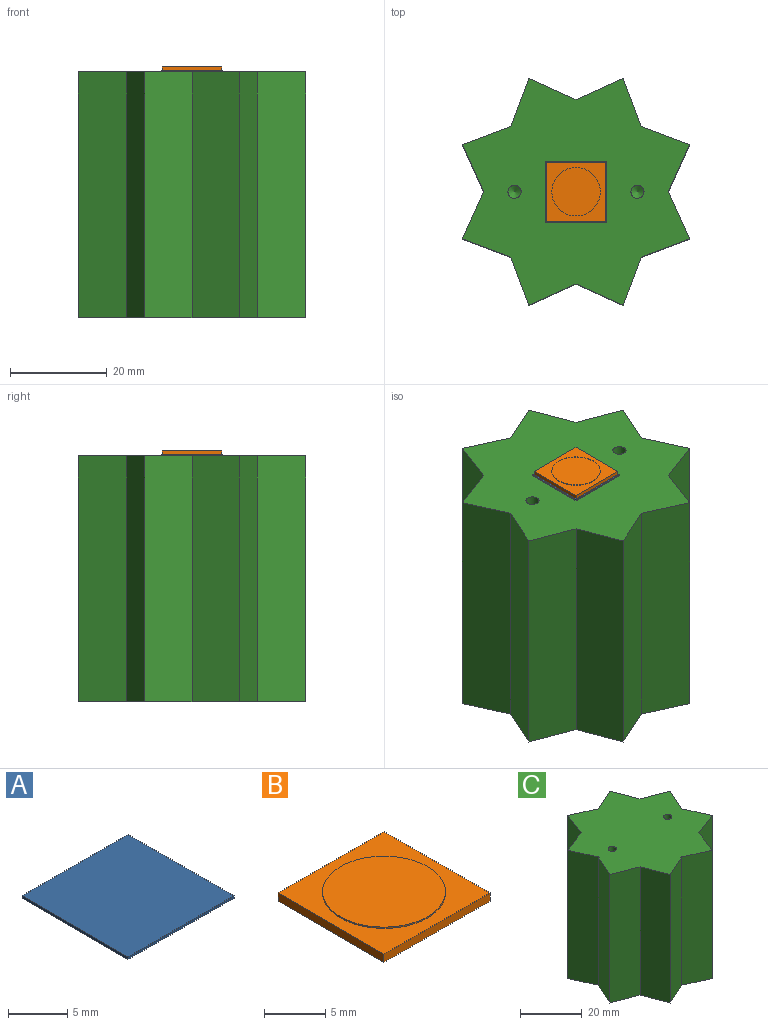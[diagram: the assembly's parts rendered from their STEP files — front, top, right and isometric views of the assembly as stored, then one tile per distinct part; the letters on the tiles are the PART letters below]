
ASSEMBLY  parts=3 mates=2
PART A: 6 faces, bbox 12.7x12.7x0.3 mm
  f0: plane 12.7x0.25mm, normal (0,1,0), area 3.2mm2, adj f1,f3,f4,f5
  f1: plane 12.7x0.25mm, normal (-1,0,0), area 3.2mm2, adj f0,f2,f4,f5
  f2: plane 12.7x0.25mm, normal (0,-1,0), area 3.2mm2, adj f1,f3,f4,f5
  f3: plane 12.7x0.25mm, normal (1,0,0), area 3.2mm2, adj f0,f2,f4,f5
  f4: plane 12.7x12.7mm, normal (0,0,1), area 161.3mm2, adj f0,f1,f2,f3
  f5: plane 12.7x12.7mm, normal (0,0,-1), area 161.3mm2, adj f0,f1,f2,f3
PART B: 8 faces, bbox 12.2x12.2x0.9 mm
  f0: plane 12.19x0.81mm, normal (0,1,0), area 9.9mm2, adj f1,f3,f4,f5
  f1: plane 12.19x0.81mm, normal (-1,0,0), area 9.9mm2, adj f0,f2,f4,f5
  f2: plane 12.19x0.81mm, normal (0,-1,0), area 9.9mm2, adj f1,f3,f4,f5
  f3: plane 12.19x0.81mm, normal (1,0,0), area 9.9mm2, adj f0,f2,f4,f5
  f4: plane 12.19x12.19mm, normal (0,0,1), area 70.1mm2, adj f0,f1,f2,f3,f6
  f5: plane 12.19x12.19mm, normal (0,0,-1), area 148.6mm2, adj f0,f1,f2,f3
  f6: cylinder r=5mm len=10mm, axis (0,0,-1), area 4mm2, adj f4,f7
  f7: plane 10x10mm, normal (0,0,1), area 78.5mm2, adj f6
PART C: 22 faces, bbox 46.9x46.9x50.8 mm
  f0: plane 50.8x10mm, normal (0.94,-0.35,0), area 542.4mm2, adj f1,f15,f16,f17
  f1: plane 50.8x10mm, normal (0.35,-0.94,0), area 542.4mm2, adj f0,f2,f16,f17
  f2: plane 50.8x9.72mm, normal (0.91,0.41,0), area 542.4mm2, adj f1,f3,f16,f17
  f3: plane 50.8x9.72mm, normal (0.91,-0.41,0), area 542.4mm2, adj f2,f4,f16,f17
  f4: plane 50.8x10mm, normal (0.35,0.94,0), area 542.4mm2, adj f3,f5,f16,f17
  f5: plane 50.8x10mm, normal (0.94,0.35,0), area 542.4mm2, adj f4,f6,f16,f17
  f6: plane 50.8x9.72mm, normal (-0.41,0.91,0), area 542.4mm2, adj f5,f7,f16,f17
  f7: plane 50.8x9.72mm, normal (0.41,0.91,0), area 542.4mm2, adj f6,f8,f16,f17
  f8: plane 50.8x10mm, normal (-0.94,0.35,0), area 542.4mm2, adj f7,f9,f16,f17
  f9: plane 50.8x10mm, normal (-0.35,0.94,0), area 542.4mm2, adj f8,f10,f16,f17
  f10: plane 50.8x9.72mm, normal (-0.91,-0.41,0), area 542.4mm2, adj f9,f11,f16,f17
  f11: plane 50.8x9.72mm, normal (-0.91,0.41,0), area 542.4mm2, adj f10,f12,f16,f17
  f12: plane 50.8x10mm, normal (-0.35,-0.94,0), area 542.4mm2, adj f11,f13,f16,f17
  f13: plane 50.8x10mm, normal (-0.94,-0.35,0), area 542.4mm2, adj f12,f14,f16,f17
  f14: plane 50.8x9.72mm, normal (0.41,-0.91,0), area 542.4mm2, adj f13,f15,f16,f17
  f15: plane 50.8x9.72mm, normal (-0.41,-0.91,0), area 542.4mm2, adj f0,f14,f16,f17
  f16: plane 46.93x46.93mm, normal (0,0,-1), area 1481.4mm2, adj f0,f1,f2,f3,f4,f5,f6,f7
  f17: plane 46.93x46.93mm, normal (0,0,1), area 1469.9mm2, adj f0,f1,f2,f3,f4,f5,f6,f7
  f18: cone r=0mm half-angle=59deg, axis (0,0,1), area 6.7mm2, adj f19
  f19: cylinder r=1.35mm len=15.08mm, axis (0,0,1), area 128.2mm2, adj f17,f18
  f20: cone r=0mm half-angle=59deg, axis (0,0,1), area 6.7mm2, adj f21
  f21: cylinder r=1.35mm len=15.08mm, axis (0,0,1), area 128.2mm2, adj f17,f20
PLACE A at identity
PLACE B at identity
PLACE C at identity
MATE fastened B.f6 <-> A.f4  axis (0,0,-1) through (0,0,0.25)mm
MATE fastened A.f5 <-> C.f17  axis (0,0,-1) through (0,0,0)mm
